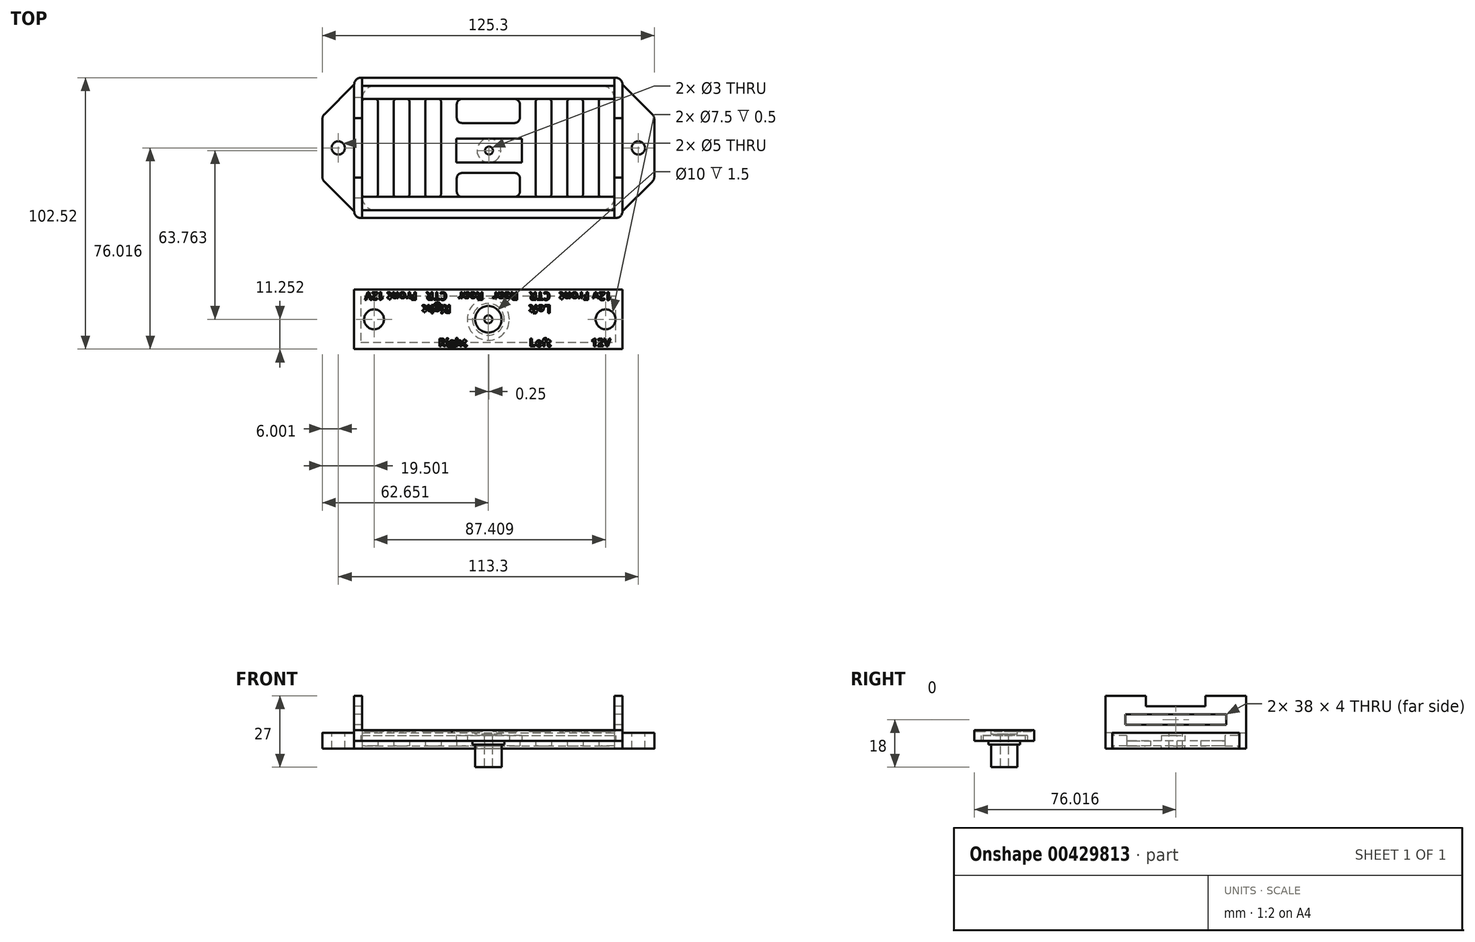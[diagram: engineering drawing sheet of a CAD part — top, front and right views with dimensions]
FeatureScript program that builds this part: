
annotation { "Feature Type Name" : "Feature", "Feature Type Description" : "" }
export const myFeature = defineFeature(function(context is Context, id is Id, definition is map)
    precondition{}
    {
        {
            var Q0;
            Q0=qCreatedBy(makeId("Top.planeOp"),FACE);
            var sketch = newSketch(context, id + "F0", { "sketchPlane" : qUnion([Q0])});
            skLineSegment(sketch, "E0.bottom", {"start": v(-46, 15.89) * mm, "end": v(49.3, 15.89) * mm});
            skLineSegment(sketch, "E0.top", {"start": v(-46, -31.11) * mm, "end": v(49.3, -31.11) * mm});
            skLineSegment(sketch, "E0.left", {"start": v(-46, 15.89) * mm, "end": v(-46, -31.11) * mm});
            skLineSegment(sketch, "E0.right", {"start": v(49.3, 15.89) * mm, "end": v(49.3, -31.11) * mm});
            skLineSegment(sketch, "E1.0", {"start": v(-46.46, -34.11) * mm, "end": v(49.76, -34.11) * mm});
            skLineSegment(sketch, "E1.1", {"start": v(-49, 16.35) * mm, "end": v(-49, -31.57) * mm});
            skLineSegment(sketch, "E1.2", {"start": v(-46.46, 18.89) * mm, "end": v(49.76, 18.89) * mm});
            skLineSegment(sketch, "E1.3", {"start": v(52.3, 16.35) * mm, "end": v(52.3, -31.57) * mm});
            skPoint(sketch, "E2.visualSharp", {"position": v(-49, 18.89) * mm});
            skArc(sketch, "E2.filletArc", {"start": v(-46.46, 18.89) * mm, "mid": v(-48.25, 18.14) * mm, "end": v(-49, 16.35) * mm});
            skPoint(sketch, "E3.visualSharp", {"position": v(-49, -34.11) * mm});
            skArc(sketch, "E3.filletArc", {"start": v(-49, -31.57) * mm, "mid": v(-48.25, -33.37) * mm, "end": v(-46.46, -34.11) * mm});
            skPoint(sketch, "E4.visualSharp", {"position": v(52.3, -34.11) * mm});
            skArc(sketch, "E4.filletArc", {"start": v(49.76, -34.11) * mm, "mid": v(51.56, -33.37) * mm, "end": v(52.3, -31.57) * mm});
            skPoint(sketch, "E5.visualSharp", {"position": v(52.3, 18.89) * mm});
            skArc(sketch, "E5.filletArc", {"start": v(52.3, 16.35) * mm, "mid": v(51.56, 18.14) * mm, "end": v(49.76, 18.89) * mm});
            skPoint(sketch, "E6.orphan", {"position": v(1.65, 15.89) * mm});
            skPoint(sketch, "E7.orphan", {"position": v(49.3, -7.61) * mm});
            skPoint(sketch, "E8.start.orphan", {"position": v(-46, -7.61) * mm});
            skLineSegment(sketch, "E9", {"start": v(14.3, -13.11) * mm, "end": v(14.3, -4.11) * mm});
            skLineSegment(sketch, "E10", {"start": v(-10.5, -4.11) * mm, "end": v(14.3, -4.11) * mm});
            skLineSegment(sketch, "E11", {"start": v(14.3, -13.11) * mm, "end": v(-10.5, -13.11) * mm});
            skLineSegment(sketch, "E12", {"start": v(-10.5, -4.11) * mm, "end": v(-10.5, -13.11) * mm});
            skLineSegment(sketch, "E13", {"start": v(-46, 10.89) * mm, "end": v(49.3, 10.89) * mm});
            skPoint(sketch, "E14.end.orphan", {"position": v(1.65, 10.89) * mm});
            skLineSegment(sketch, "E15", {"start": v(1.65, -31.11) * mm, "end": v(1.65, -26.11) * mm});
            skLineSegment(sketch, "E16", {"start": v(-46, -26.11) * mm, "end": v(49.3, -26.11) * mm});
            skLineSegment(sketch, "E17", {"start": v(49.3, 15.89) * mm, "end": v(49.3, 18.89) * mm});
            skLineSegment(sketch, "E18", {"start": v(-46, 15.89) * mm, "end": v(-46, 18.89) * mm});
            skLineSegment(sketch, "E19", {"start": v(49.3, -31.11) * mm, "end": v(49.3, -34.11) * mm});
            skLineSegment(sketch, "E20", {"start": v(-46, -31.11) * mm, "end": v(-46, -34.11) * mm});
            skCircle(sketch, "E21", {"center": v(1.9, -8.61) * mm, "radius": 1.5 * mm});
            skPoint(sketch, "E22.orphan", {"position": v(1.9, -13.11) * mm});
            skPoint(sketch, "E23.end.orphan", {"position": v(1.9, -4.11) * mm});
            skLineSegment(sketch, "E24.bottom", {"start": v(52.3, -61.13) * mm, "end": v(-49, -61.13) * mm});
            skLineSegment(sketch, "E24.top", {"start": v(52.3, -83.63) * mm, "end": v(-49, -83.63) * mm});
            skLineSegment(sketch, "E24.left", {"start": v(52.3, -61.13) * mm, "end": v(52.3, -83.63) * mm});
            skLineSegment(sketch, "E24.right", {"start": v(-49, -61.13) * mm, "end": v(-49, -83.63) * mm});
            skCircle(sketch, "E25", {"center": v(1.65, -72.38) * mm, "radius": 1.5 * mm});
            skPoint(sketch, "E26.orphan", {"position": v(1.65, -83.63) * mm});
            skPoint(sketch, "E27.orphan", {"position": v(1.65, -61.13) * mm});
            skCircle(sketch, "E28", {"center": v(1.65, -72.38) * mm, "radius": 5 * mm});
            skLineSegment(sketch, "E29.right", {"start": v(-61, 3.31) * mm, "end": v(-61, -18.54) * mm});
            skLineSegment(sketch, "E30.right", {"start": v(64.3, 3.31) * mm, "end": v(64.3, -7.61) * mm});
            skLineSegment(sketch, "E31", {"start": v(64.3, -7.61) * mm, "end": v(64.3, -18.54) * mm});
            skLineSegment(sketch, "E32", {"start": v(52.3, 16.35) * mm, "end": v(63.56, 5.1) * mm});
            skLineSegment(sketch, "E33", {"start": v(63.56, -20.34) * mm, "end": v(52.3, -31.57) * mm});
            skLineSegment(sketch, "E34", {"start": v(-49, 16.35) * mm, "end": v(-60.25, 5.1) * mm});
            skLineSegment(sketch, "E35", {"start": v(-60.25, -20.34) * mm, "end": v(-49, -31.57) * mm});
            skPoint(sketch, "E36.orphan", {"position": v(-61, 16.35) * mm});
            skPoint(sketch, "E29.top.end.orphan", {"position": v(-61, -31.57) * mm});
            skPoint(sketch, "E37.orphan", {"position": v(64.3, 16.35) * mm});
            skPoint(sketch, "E38.orphan", {"position": v(64.3, -31.57) * mm});
            skPoint(sketch, "E39.end.orphan", {"position": v(52.3, -7.61) * mm});
            skPoint(sketch, "E40.end.orphan", {"position": v(-49, -7.61) * mm});
            skPoint(sketch, "E41.visualSharp", {"position": v(64.3, 4.37) * mm});
            skArc(sketch, "E41.filletArc", {"start": v(64.3, 3.31) * mm, "mid": v(64.1, 4.29) * mm, "end": v(63.56, 5.1) * mm});
            skPoint(sketch, "E42.visualSharp", {"position": v(64.3, -19.6) * mm});
            skArc(sketch, "E42.filletArc", {"start": v(63.56, -20.34) * mm, "mid": v(64.1, -19.51) * mm, "end": v(64.3, -18.54) * mm});
            skPoint(sketch, "E43.start.orphan", {"position": v(-61, -7.61) * mm});
            skPoint(sketch, "E44.visualSharp", {"position": v(-61, 4.37) * mm});
            skArc(sketch, "E44.filletArc", {"start": v(-60.25, 5.1) * mm, "mid": v(-60.8, 4.29) * mm, "end": v(-61, 3.31) * mm});
            skPoint(sketch, "E45.visualSharp", {"position": v(-61, -19.6) * mm});
            skArc(sketch, "E45.filletArc", {"start": v(-61, -18.54) * mm, "mid": v(-60.8, -19.51) * mm, "end": v(-60.25, -20.34) * mm});
            skCircle(sketch, "E46", {"center": v(-55, -7.61) * mm, "radius": 2.5 * mm});
            skCircle(sketch, "E47", {"center": v(58.3, -7.61) * mm, "radius": 2.5 * mm});
            skSolve(sketch);
        }
        {
            var Q0;
            Q0=makeQuery(id+"F0.imprint","IMPRINT",FACE,{"disambiguationData":[TD([[makeQuery(id+"F0.imprint","IMPRINT",EDGE,{"derivedFrom":sQuery(id+"F0.wireOp",EDGE,"E0.bottom")}),-1.0]])]});
            var Q1;
            Q1=makeQuery(id+"F0.imprint","IMPRINT",FACE,{"disambiguationData":[TD([[makeQuery(id+"F0.imprint","IMPRINT",EDGE,{"derivedFrom":sQuery(id+"F0.wireOp",EDGE,"E0.bottom")}),1.0]])]});
            var Q2;
            Q2=makeQuery(id+"F0.imprint","IMPRINT",FACE,{"disambiguationData":[TD([[makeQuery(id+"F0.imprint","IMPRINT",EDGE,{"derivedFrom":sQuery(id+"F0.wireOp",EDGE,"269553c9-e765-4ec5-81e7-e4e1725ccf4f.0")}),-1.0]])]});
            var Q3;
            Q3=makeQuery(id+"F0.imprint","IMPRINT",FACE,{"disambiguationData":[TD([[makeQuery(id+"F0.imprint","IMPRINT",EDGE,{"derivedFrom":sQuery(id+"F0.wireOp",EDGE,"E9")}),1.0]])]});
            var Q4;
            Q4=makeQuery(id+"F0.imprint","IMPRINT",FACE,{"disambiguationData":[TD([[makeQuery(id+"F0.imprint","IMPRINT",EDGE,{"derivedFrom":sQuery(id+"F0.wireOp",EDGE,"E9")}),-1.0]])]});
            var Q5;
            {var subQ3=sQuery(id+"F0.wireOp",EDGE,"E15");Q5=makeQuery(id+"F0.imprint","IMPRINT",FACE,{"disambiguationData":[TD([[makeQuery(id+"F0.imprint","IMPRINT",EDGE,{"derivedFrom":subQ3}),1.0]])]});}
            var Q6;
            {var subQ3=sQuery(id+"F0.wireOp",EDGE,"E15");Q6=makeQuery(id+"F0.imprint","IMPRINT",FACE,{"disambiguationData":[TD([[makeQuery(id+"F0.imprint","IMPRINT",EDGE,{"derivedFrom":subQ3}),-1.0]])]});}
            var Q7;
            {var subQ0=sQuery(id+"F0.wireOp",EDGE,"E19");Q7=makeQuery(id+"F0.imprint","IMPRINT",FACE,{"disambiguationData":[TD([[makeQuery(id+"F0.imprint","IMPRINT",EDGE,{"derivedFrom":subQ0}),-1.0]])]});}
            var Q8;
            Q8=makeQuery(id+"F0.imprint","IMPRINT",FACE,{"disambiguationData":[TD([[makeQuery(id+"F0.imprint","IMPRINT",EDGE,{"derivedFrom":sQuery(id+"F0.wireOp",EDGE,"E1.3")}),-1.0]])]});
            var Q9;
            Q9=makeQuery(id+"F0.imprint","IMPRINT",FACE,{"disambiguationData":[TD([[makeQuery(id+"F0.imprint","IMPRINT",EDGE,{"derivedFrom":sQuery(id+"F0.wireOp",EDGE,"E1.1")}),1.0]])]});
            var Q10;
            {var subQ6=sQuery(id+"F0.wireOp",EDGE,"E2.filletArc");Q10=makeQuery(id+"F0.imprint","IMPRINT",FACE,{"disambiguationData":[TD([[makeQuery(id+"F0.imprint","IMPRINT",EDGE,{"derivedFrom":subQ6}),1.0]])]});}
            var Q11;
            {var subQ5=sQuery(id+"F0.wireOp",EDGE,"E4.filletArc");Q11=makeQuery(id+"F0.imprint","IMPRINT",FACE,{"disambiguationData":[TD([[makeQuery(id+"F0.imprint","IMPRINT",EDGE,{"derivedFrom":subQ5}),1.0]])]});}
            var Q12;
            Q12=makeQuery(id+"F0.imprint","IMPRINT",FACE,{"disambiguationData":[TD([[makeQuery(id+"F0.imprint","IMPRINT",EDGE,{"derivedFrom":sQuery(id+"F0.wireOp",EDGE,"E1.1")}),-1.0]])]});
            var Q13;
            Q13=makeQuery(id+"F0.imprint","IMPRINT",FACE,{"disambiguationData":[TD([[makeQuery(id+"F0.imprint","IMPRINT",EDGE,{"derivedFrom":sQuery(id+"F0.wireOp",EDGE,"E1.3")}),1.0]])]});
            extrude(context, id + "F1", {"entities" : qUnion([Q0, Q1, Q2, Q3, Q4, Q5, Q6, Q7, Q8, Q9, Q10, Q11, Q12, Q13]), "oppositeDirection" : true, "depth" : 3 * mm});
        }
        {
            var Q0;
            Q0=makeQuery(id+"F0.imprint","IMPRINT",FACE,{"disambiguationData":[TD([[makeQuery(id+"F0.imprint","IMPRINT",EDGE,{"derivedFrom":sQuery(id+"F0.wireOp",EDGE,"E1.3")}),-1.0]])]});
            var Q1;
            Q1=makeQuery(id+"F0.imprint","IMPRINT",FACE,{"disambiguationData":[TD([[makeQuery(id+"F0.imprint","IMPRINT",EDGE,{"derivedFrom":sQuery(id+"F0.wireOp",EDGE,"E1.1")}),1.0]])]});
            var Q2;
            {var subQ6=sQuery(id+"F0.wireOp",EDGE,"E2.filletArc");Q2=makeQuery(id+"F0.imprint","IMPRINT",FACE,{"disambiguationData":[TD([[makeQuery(id+"F0.imprint","IMPRINT",EDGE,{"derivedFrom":subQ6}),1.0]])]});}
            var Q3;
            {var subQ5=sQuery(id+"F0.wireOp",EDGE,"E4.filletArc");Q3=makeQuery(id+"F0.imprint","IMPRINT",FACE,{"disambiguationData":[TD([[makeQuery(id+"F0.imprint","IMPRINT",EDGE,{"derivedFrom":subQ5}),1.0]])]});}
            extrude(context, id + "F2", {"entities" : qUnion([Q0, Q1, Q2, Q3]), "operationType" : NewBodyOperationType.ADD, "depth" : 17 * mm});
        }
        {
            var Q0;
            Q0=makeQuery(id+"F0.imprint","IMPRINT",FACE,{"disambiguationData":[TD([[makeQuery(id+"F0.imprint","IMPRINT",EDGE,{"derivedFrom":sQuery(id+"F0.wireOp",EDGE,"E9")}),1.0]])]});
            var Q1;
            {var subQ0=sQuery(id+"F0.wireOp",EDGE,"E0.bottom");Q1=makeQuery(id+"F0.imprint","IMPRINT",FACE,{"disambiguationData":[TD([[makeQuery(id+"F0.imprint","IMPRINT",EDGE,{"derivedFrom":subQ0}),-1.0]])]});}
            var Q2;
            {var subQ3=sQuery(id+"F0.wireOp",EDGE,"E15");Q2=makeQuery(id+"F0.imprint","IMPRINT",FACE,{"disambiguationData":[TD([[makeQuery(id+"F0.imprint","IMPRINT",EDGE,{"derivedFrom":subQ3}),1.0]])]});}
            var Q3;
            {var subQ3=sQuery(id+"F0.wireOp",EDGE,"E15");Q3=makeQuery(id+"F0.imprint","IMPRINT",FACE,{"disambiguationData":[TD([[makeQuery(id+"F0.imprint","IMPRINT",EDGE,{"derivedFrom":subQ3}),-1.0]])]});}
            extrude(context, id + "F3", {"entities" : qUnion([Q0, Q1, Q2, Q3]), "operationType" : NewBodyOperationType.ADD, "depth" : 2 * mm});
        }
        {
            var Q0;
            Q0=makeQuery(id+"F0.imprint","IMPRINT",FACE,{"disambiguationData":[TD([[makeQuery(id+"F0.imprint","IMPRINT",EDGE,{"derivedFrom":sQuery(id+"F0.wireOp",EDGE,"E0.bottom")}),1.0]])]});
            var Q1;
            {var subQ0=sQuery(id+"F0.wireOp",EDGE,"E19");Q1=makeQuery(id+"F0.imprint","IMPRINT",FACE,{"disambiguationData":[TD([[makeQuery(id+"F0.imprint","IMPRINT",EDGE,{"derivedFrom":subQ0}),-1.0]])]});}
            extrude(context, id + "F4", {"entities" : qUnion([Q0, Q1]), "operationType" : NewBodyOperationType.ADD, "depth" : 3 * mm});
        }
        {
            var Q0;
            Q0=makeQuery(id+"F2.opExtrude","CAP_FACE",FACE,{"disambiguationData":[OSD([sQuery(id+"F0.wireOp",EDGE,"E0.right"),sQuery(id+"F0.wireOp",EDGE,"E1.0"),sQuery(id+"F0.wireOp",EDGE,"E1.2"),sQuery(id+"F0.wireOp",EDGE,"E1.3"),sQuery(id+"F0.wireOp",EDGE,"E4.filletArc"),sQuery(id+"F0.wireOp",EDGE,"E5.filletArc"),sQuery(id+"F0.wireOp",EDGE,"E17"),sQuery(id+"F0.wireOp",EDGE,"E19")])],"isStart":false});
            var sketch = newSketch(context, id + "F5", { "sketchPlane" : qUnion([Q0])});
            skPoint(sketch, "E48.orphan", {"position": v(49.3, -34.11) * mm});
            skPoint(sketch, "E49.orphan", {"position": v(52.3, -31.57) * mm});
            skPoint(sketch, "E50.1.start.orphan", {"position": v(52.3, 16.35) * mm});
            skPoint(sketch, "E50.0.end.orphan", {"position": v(49.3, 18.89) * mm});
            skLineSegment(sketch, "E51", {"start": v(52.3, -18.86) * mm, "end": v(52.3, 3.64) * mm});
            skLineSegment(sketch, "E52", {"start": v(52.3, 3.64) * mm, "end": v(49.3, 3.64) * mm});
            skLineSegment(sketch, "E53", {"start": v(49.3, -18.86) * mm, "end": v(52.3, -18.86) * mm});
            skPoint(sketch, "E54.end.orphan", {"position": v(52.3, -7.61) * mm});
            skPoint(sketch, "E55.start.orphan", {"position": v(49.3, -7.61) * mm});
            skLineSegment(sketch, "E56", {"start": v(49.3, -18.86) * mm, "end": v(49.3, 3.64) * mm});
            skSolve(sketch);
        }
        {
            var Q0;
            Q0=makeQuery(id+"F2.opExtrude","CAP_FACE",FACE,{"disambiguationData":[OSD([sQuery(id+"F0.wireOp",EDGE,"E0.left"),sQuery(id+"F0.wireOp",EDGE,"E1.0"),sQuery(id+"F0.wireOp",EDGE,"E1.1"),sQuery(id+"F0.wireOp",EDGE,"E1.2"),sQuery(id+"F0.wireOp",EDGE,"E2.filletArc"),sQuery(id+"F0.wireOp",EDGE,"E3.filletArc"),sQuery(id+"F0.wireOp",EDGE,"E18"),sQuery(id+"F0.wireOp",EDGE,"E20")])],"isStart":false});
            var sketch = newSketch(context, id + "F6", { "sketchPlane" : qUnion([Q0])});
            skLineSegment(sketch, "E57.0", {"start": v(-46, 18.89) * mm, "end": v(-46, -34.11) * mm});
            skLineSegment(sketch, "E58", {"start": v(-46, 3.64) * mm, "end": v(-49, 3.64) * mm});
            skLineSegment(sketch, "E59", {"start": v(-49, 3.64) * mm, "end": v(-49, -18.86) * mm});
            skLineSegment(sketch, "E60", {"start": v(-49, -18.86) * mm, "end": v(-46, -18.86) * mm});
            skPoint(sketch, "E61.end.orphan", {"position": v(-49, -7.61) * mm});
            skPoint(sketch, "E62.start.orphan", {"position": v(-46, -7.61) * mm});
            skLineSegment(sketch, "E63", {"start": v(-46, 3.64) * mm, "end": v(-46, -18.86) * mm});
            skSolve(sketch);
        }
        {
            var Q0;
            Q0=makeQuery(id+"F5.imprint","IMPRINT",FACE,{"disambiguationData":[TD([[makeQuery(id+"F5.imprint","IMPRINT",EDGE,{"derivedFrom":sQuery(id+"F5.wireOp",EDGE,"E51")}),-1.0]])]});
            var Q1;
            Q1=makeQuery(id+"F6.imprint","IMPRINT",FACE,{"disambiguationData":[TD([[makeQuery(id+"F6.imprint","IMPRINT",EDGE,{"derivedFrom":sQuery(id+"F6.wireOp",EDGE,"E58")}),1.0]])]});
            extrude(context, id + "F7", {"entities" : qUnion([Q0, Q1]), "operationType" : NewBodyOperationType.REMOVE, "oppositeDirection" : true, "depth" : 4 * mm});
        }
        {
            var Q0;
            Q0=makeQuery(id+"F0.imprint","IMPRINT",FACE,{"disambiguationData":[TD([[makeQuery(id+"F0.imprint","IMPRINT",EDGE,{"derivedFrom":sQuery(id+"F0.wireOp",EDGE,"E24.bottom")}),1.0]])]});
            var Q1;
            Q1=makeQuery(id+"F0.imprint","IMPRINT",FACE,{"disambiguationData":[TD([[makeQuery(id+"F0.imprint","IMPRINT",EDGE,{"derivedFrom":sQuery(id+"F0.wireOp",EDGE,"E25")}),-1.0]])]});
            extrude(context, id + "F8", {"entities" : qUnion([Q0, Q1]), "depth" : 4 * mm});
        }
        {
            var Q0;
            Q0=makeQuery(id+"F0.imprint","IMPRINT",FACE,{"disambiguationData":[TD([[makeQuery(id+"F0.imprint","IMPRINT",EDGE,{"derivedFrom":sQuery(id+"F0.wireOp",EDGE,"E25")}),-1.0]])]});
            extrude(context, id + "F9", {"entities" : qUnion([Q0]), "operationType" : NewBodyOperationType.ADD, "oppositeDirection" : true, "depth" : 10 * mm});
        }
        {
            var Q0;
            Q0=makeQuery(id+"F0.imprint","IMPRINT",FACE,{"disambiguationData":[TD([[makeQuery(id+"F0.imprint","IMPRINT",EDGE,{"derivedFrom":sQuery(id+"F0.wireOp",EDGE,"E1.1")}),-1.0]])]});
            var Q1;
            Q1=makeQuery(id+"F0.imprint","IMPRINT",FACE,{"disambiguationData":[TD([[makeQuery(id+"F0.imprint","IMPRINT",EDGE,{"derivedFrom":sQuery(id+"F0.wireOp",EDGE,"E1.3")}),1.0]])]});
            extrude(context, id + "F10", {"entities" : qUnion([Q0, Q1]), "operationType" : NewBodyOperationType.ADD, "depth" : 3 * mm});
        }
        {
            var Q0;
            Q0=makeQuery(id+"F8.opExtrude","CAP_FACE",FACE,{"disambiguationData":[OSD([sQuery(id+"F0.wireOp",EDGE,"E24.bottom"),sQuery(id+"F0.wireOp",EDGE,"E24.top"),sQuery(id+"F0.wireOp",EDGE,"E24.left"),sQuery(id+"F0.wireOp",EDGE,"E24.right"),sQuery(id+"F0.wireOp",EDGE,"E25")])],"isStart":false});
            var sketch = newSketch(context, id + "F11", { "sketchPlane" : qUnion([Q0])});
            skCircle(sketch, "E64.0", {"center": v(1.65, -72.38) * mm, "radius": 5 * mm});
            skSolve(sketch);
        }
        {
            var Q0;
            Q0=makeQuery(id+"F11.imprint","IMPRINT",FACE,{"disambiguationData":[TD([[makeQuery(id+"F11.imprint","IMPRINT",EDGE,{"derivedFrom":sQuery(id+"F11.wireOp",EDGE,"E64.0")}),1.0]])]});
            extrude(context, id + "F12", {"entities" : qUnion([Q0]), "operationType" : NewBodyOperationType.REMOVE, "oppositeDirection" : true, "depth" : 1.5 * mm});
        }
        {
            var Q0;
            Q0=makeQuery(id+"F0.imprint","IMPRINT",FACE,{"disambiguationData":[TD([[makeQuery(id+"F0.imprint","IMPRINT",EDGE,{"derivedFrom":sQuery(id+"F0.wireOp",EDGE,"E24.bottom")}),1.0]])]});
            var sketch = newSketch(context, id + "F13", { "sketchPlane" : qUnion([Q0])});
            skCircle(sketch, "E65.0", {"center": v(1.65, -72.38) * mm, "radius": 5 * mm});
            skCircle(sketch, "E66.0", {"center": v(1.65, -72.38) * mm, "radius": 6 * mm});
            skSolve(sketch);
        }
        {
            var Q0;
            Q0=makeQuery(id+"F13.imprint","IMPRINT",FACE,{"disambiguationData":[TD([[makeQuery(id+"F13.imprint","IMPRINT",EDGE,{"derivedFrom":sQuery(id+"F13.wireOp",EDGE,"E65.0")}),-1.0]])]});
            extrude(context, id + "F14", {"entities" : qUnion([Q0]), "operationType" : NewBodyOperationType.ADD, "oppositeDirection" : true, "depth" : 1.5 * mm});
        }
        {
            var Q0;
            Q0=makeQuery(id+"F8.opExtrude","CAP_FACE",FACE,{"disambiguationData":[OSD([sQuery(id+"F0.wireOp",EDGE,"E24.bottom"),sQuery(id+"F0.wireOp",EDGE,"E24.top"),sQuery(id+"F0.wireOp",EDGE,"E24.left"),sQuery(id+"F0.wireOp",EDGE,"E24.right"),sQuery(id+"F0.wireOp",EDGE,"E25")])],"isStart":false});
            var sketch = newSketch(context, id + "F15", { "sketchPlane" : qUnion([Q0])});
            skLineSegment(sketch, "E67", {"start": v(-49, -61.13) * mm, "end": v(-46, -61.13) * mm});
            skLineSegment(sketch, "E68", {"start": v(-46, -61.13) * mm, "end": v(-36, -61.13) * mm});
            skLineSegment(sketch, "E69", {"start": v(-36, -61.13) * mm, "end": v(-26, -61.13) * mm});
            skLineSegment(sketch, "E70", {"start": v(-26, -61.13) * mm, "end": v(-23, -61.13) * mm});
            skLineSegment(sketch, "E71", {"start": v(-23, -61.13) * mm, "end": v(-13, -61.13) * mm});
            skLineSegment(sketch, "E72", {"start": v(-13, -61.13) * mm, "end": v(-10, -61.13) * mm});
            skLineSegment(sketch, "E73", {"start": v(-10, -61.13) * mm, "end": v(0, -61.13) * mm});
            skLineSegment(sketch, "E74", {"start": v(0, -61.13) * mm, "end": v(3, -61.13) * mm});
            skLineSegment(sketch, "E75", {"start": v(3, -61.13) * mm, "end": v(13, -61.13) * mm});
            skLineSegment(sketch, "E76", {"start": v(13, -61.13) * mm, "end": v(16, -61.13) * mm});
            skLineSegment(sketch, "E77", {"start": v(16, -61.13) * mm, "end": v(26, -61.13) * mm});
            skLineSegment(sketch, "E78", {"start": v(26, -61.13) * mm, "end": v(29, -61.13) * mm});
            skLineSegment(sketch, "E79", {"start": v(29, -61.13) * mm, "end": v(39, -61.13) * mm});
            skLineSegment(sketch, "E80", {"start": v(39, -61.13) * mm, "end": v(49, -61.13) * mm});
            skLineSegment(sketch, "E81", {"start": v(52.3, -83.63) * mm, "end": v(49.3, -83.63) * mm});
            skLineSegment(sketch, "E82", {"start": v(49.3, -83.63) * mm, "end": v(39.3, -83.63) * mm});
            skLineSegment(sketch, "E83", {"start": v(39.3, -83.63) * mm, "end": v(26.3, -83.63) * mm});
            skLineSegment(sketch, "E84", {"start": v(26.3, -83.63) * mm, "end": v(16.3, -83.63) * mm});
            skLineSegment(sketch, "E85", {"start": v(16.3, -83.63) * mm, "end": v(-6.7, -83.63) * mm});
            skLineSegment(sketch, "E86", {"start": v(-6.7, -83.63) * mm, "end": v(-16.7, -83.63) * mm});
            skPoint(sketch, "E87.middle", {"position": v(44, -61.13) * mm});
            skText(sketch, "E88", { "text": "12v", "fontName": "OpenSans-Bold.ttf"});
            skPoint(sketch, "E89.start.orphan", {"position": v(34, -61.13) * mm});
            skPoint(sketch, "E90.start.orphan", {"position": v(21, -61.13) * mm});
            skLineSegment(sketch, "E91", {"start": v(44, -61.13) * mm, "end": v(44, -62.13) * mm});
            skLineSegment(sketch, "E92", {"start": v(34, -61.13) * mm, "end": v(34, -62.13) * mm});
            skLineSegment(sketch, "E93", {"start": v(21, -61.13) * mm, "end": v(21, -62.13) * mm});
            skPoint(sketch, "E94.start.orphan", {"position": v(-5, -61.13) * mm});
            skPoint(sketch, "E95.start.orphan", {"position": v(-41, -61.13) * mm});
            skPoint(sketch, "E96.start.orphan", {"position": v(-31, -61.13) * mm});
            skPoint(sketch, "E97.start.orphan", {"position": v(-18, -61.13) * mm});
            skPoint(sketch, "E98.start.orphan", {"position": v(8, -61.13) * mm});
            skLineSegment(sketch, "E99", {"start": v(8, -61.13) * mm, "end": v(8, -62.13) * mm});
            skLineSegment(sketch, "E100", {"start": v(-5, -61.13) * mm, "end": v(-5, -62.13) * mm});
            skLineSegment(sketch, "E101", {"start": v(-18, -61.13) * mm, "end": v(-18, -62.13) * mm});
            skLineSegment(sketch, "E102", {"start": v(-31, -61.13) * mm, "end": v(-31, -62.13) * mm});
            skLineSegment(sketch, "E103", {"start": v(-41, -61.13) * mm, "end": v(-41, -62.13) * mm});
            skLineSegment(sketch, "E104", {"start": v(34.62, -51.7) * mm, "end": v(26.62, -51.7) * mm});
            skLineSegment(sketch, "E105", {"start": v(26.62, -51.7) * mm, "end": v(26.62, -48.7) * mm});
            skText(sketch, "E106", { "text": "Front\n", "fontName": "OpenSans-Bold.ttf"});
            skText(sketch, "E107", { "text": "Rear", "fontName": "OpenSans-Bold.ttf"});
            skText(sketch, "E108", { "text": "CTR", "fontName": "OpenSans-Bold.ttf"});
            skLineSegment(sketch, "E109", {"start": v(21, -65.13) * mm, "end": v(21, -67) * mm});
            skText(sketch, "E110", { "text": "Left", "fontName": "OpenSans-Bold.ttf"});
            skText(sketch, "E111", { "text": "Rear", "fontName": "OpenSans-Bold.ttf"});
            skText(sketch, "E112", { "text": "CTR", "fontName": "OpenSans-Bold.ttf"});
            skText(sketch, "E113", { "text": "Front", "fontName": "OpenSans-Bold.ttf"});
            skText(sketch, "E114", { "text": "12V", "fontName": "OpenSans-Bold.ttf"});
            skLineSegment(sketch, "E115", {"start": v(-18, -65.13) * mm, "end": v(-18, -67) * mm});
            skText(sketch, "E116", { "text": "Right", "fontName": "OpenSans-Bold.ttf"});
            skText(sketch, "E117", { "text": "12V", "fontName": "OpenSans-Bold.ttf"});
            skLineSegment(sketch, "E118", {"start": v(44.3, -83.63) * mm, "end": v(44.3, -82.63) * mm});
            skLineSegment(sketch, "E119", {"start": v(21.3, -83.63) * mm, "end": v(21.3, -82.63) * mm});
            skLineSegment(sketch, "E120", {"start": v(-11.7, -83.63) * mm, "end": v(-11.7, -82.63) * mm});
            skText(sketch, "E121", { "text": "Left", "fontName": "OpenSans-Bold.ttf"});
            skText(sketch, "E122", { "text": "Right", "fontName": "OpenSans-Bold.ttf"});
            skLineSegment(sketch, "E123", {"start": v(26.3, -83.63) * mm, "end": v(39.3, -83.63) * mm});
            skLineSegment(sketch, "E124", {"start": v(32.8, -83.63) * mm, "end": v(32.8, -81.9) * mm});
            skLineSegment(sketch, "E125", {"start": v(32.8, -83.63) * mm, "end": v(27.8, -83.63) * mm});
            skLineSegment(sketch, "E126", {"start": v(32.8, -83.63) * mm, "end": v(37.8, -83.63) * mm});
            skLineSegment(sketch, "E127", {"start": v(27.8, -83.63) * mm, "end": v(27.8, -90.63) * mm});
            skLineSegment(sketch, "E128", {"start": v(37.8, -83.63) * mm, "end": v(37.8, -90.63) * mm});
            skLineSegment(sketch, "E129", {"start": v(37.8, -90.63) * mm, "end": v(27.8, -90.63) * mm});
            skLineSegment(sketch, "E130", {"start": v(4.8, -83.63) * mm, "end": v(4.8, -81.9) * mm});
            skLineSegment(sketch, "E131", {"start": v(4.8, -83.63) * mm, "end": v(-5.2, -83.63) * mm});
            skLineSegment(sketch, "E132", {"start": v(4.8, -83.63) * mm, "end": v(14.8, -83.63) * mm});
            skLineSegment(sketch, "E133", {"start": v(-49, -83.63) * mm, "end": v(-46, -83.63) * mm});
            skLineSegment(sketch, "E134", {"start": v(-46, -83.63) * mm, "end": v(-16.7, -83.63) * mm});
            skLineSegment(sketch, "E135", {"start": v(-31.35, -83.63) * mm, "end": v(-43.35, -83.63) * mm});
            skLineSegment(sketch, "E136", {"start": v(-31.35, -83.63) * mm, "end": v(-19.35, -83.63) * mm});
            skLineSegment(sketch, "E137", {"start": v(-43.35, -83.63) * mm, "end": v(-43.35, -90.63) * mm});
            skLineSegment(sketch, "E138", {"start": v(-19.35, -83.63) * mm, "end": v(-19.35, -90.63) * mm});
            skLineSegment(sketch, "E139", {"start": v(-19.35, -90.63) * mm, "end": v(-43.35, -90.63) * mm});
            skLineSegment(sketch, "E140", {"start": v(-5.2, -83.63) * mm, "end": v(-5.2, -90.63) * mm});
            skLineSegment(sketch, "E141", {"start": v(14.8, -83.63) * mm, "end": v(14.8, -90.63) * mm});
            skLineSegment(sketch, "E142", {"start": v(14.8, -90.63) * mm, "end": v(-5.2, -90.63) * mm});
            skLineSegment(sketch, "E143", {"start": v(-49, -72.38) * mm, "end": v(-41.5, -72.38) * mm});
            skPoint(sketch, "E143.endSnap0", {"position": v(-41.5, -63.61) * mm});
            skCircle(sketch, "E144", {"center": v(-41.5, -72.38) * mm, "radius": 3.75 * mm});
            skLineSegment(sketch, "E145", {"start": v(52.3, -72.38) * mm, "end": v(45.9, -72.38) * mm});
            skCircle(sketch, "E146", {"center": v(45.9, -72.38) * mm, "radius": 3.75 * mm});
            const initialGuessF15  = {"E88": [0.04828, -0.06213, -1, 0, 0.00306], "E106": [0.03972, -0.06213, -1, 0, 0.003], "E107": [0.0129, -0.06213, -1, 0, 0.003], "E108": [0.02505, -0.06213, -1, 0, 0.003], "E110": [0.02519, -0.067, -1, 0, 0.003], "E111": [-0.0001, -0.06213, -1, 0, 0.003], "E112": [-0.01395, -0.06213, -1, 0, 0.003], "E113": [-0.02528, -0.06213, -1, 0, 0.003], "E114": [-0.03775, -0.06216, -1, 0, 0.0029], "E116": [-0.01247, -0.067, -1, 0, 0.003], "E117": [0.04043, -0.08263, 1, 0, 0.003], "E121": [0.01711, -0.08263, 1, 0, 0.003], "E122": [-0.01723, -0.08263, 1, 0, 0.003]};
            skSetInitialGuess(sketch, initialGuessF15);
            skSolve(sketch);
        }
        {
            var Q0;
            Q0=makeQuery(id+"F15.imprint","IMPRINT",FACE,{"disambiguationData":[TD([[makeQuery(id+"F15.imprint","IMPRINT",EDGE,{"derivedFrom":sQuery(id+"F15.wireOp",EDGE,"E88.sketch_text.stroke-0")}),-1.0]])]});
            var Q1;
            {var subQ0=sQuery(id+"F15.wireOp",EDGE,"E88.sketch_text.stroke-11");Q1=makeQuery(id+"F15.imprint","IMPRINT",FACE,{"disambiguationData":[TD([[makeQuery(id+"F15.imprint","IMPRINT",EDGE,{"derivedFrom":subQ0}),-1.0]])]});}
            var Q2;
            Q2=makeQuery(id+"F15.imprint","IMPRINT",FACE,{"disambiguationData":[TD([[makeQuery(id+"F15.imprint","IMPRINT",EDGE,{"derivedFrom":sQuery(id+"F15.wireOp",EDGE,"E88.sketch_text.stroke-34")}),-1.0]])]});
            var Q3;
            Q3=makeQuery(id+"F15.imprint","IMPRINT",FACE,{"disambiguationData":[TD([[makeQuery(id+"F15.imprint","IMPRINT",EDGE,{"derivedFrom":sQuery(id+"F15.wireOp",EDGE,"E106.sketch_text.stroke-0")}),-1.0]])]});
            var Q4;
            Q4=makeQuery(id+"F15.imprint","IMPRINT",FACE,{"disambiguationData":[TD([[makeQuery(id+"F15.imprint","IMPRINT",EDGE,{"derivedFrom":sQuery(id+"F15.wireOp",EDGE,"E106.sketch_text.stroke-10")}),-1.0]])]});
            var Q5;
            Q5=makeQuery(id+"F15.imprint","IMPRINT",FACE,{"disambiguationData":[TD([[makeQuery(id+"F15.imprint","IMPRINT",EDGE,{"derivedFrom":sQuery(id+"F15.wireOp",EDGE,"E106.sketch_text.stroke-23")}),-1.0]])]});
            var Q6;
            Q6=makeQuery(id+"F15.imprint","IMPRINT",FACE,{"disambiguationData":[TD([[makeQuery(id+"F15.imprint","IMPRINT",EDGE,{"derivedFrom":sQuery(id+"F15.wireOp",EDGE,"E106.sketch_text.stroke-58")}),-1.0]])]});
            var Q7;
            Q7=makeQuery(id+"F15.imprint","IMPRINT",FACE,{"disambiguationData":[TD([[makeQuery(id+"F15.imprint","IMPRINT",EDGE,{"derivedFrom":sQuery(id+"F15.wireOp",EDGE,"E106.sketch_text.stroke-41")}),-1.0]])]});
            var Q8;
            Q8=makeQuery(id+"F15.imprint","IMPRINT",FACE,{"disambiguationData":[TD([[makeQuery(id+"F15.imprint","IMPRINT",EDGE,{"derivedFrom":sQuery(id+"F15.wireOp",EDGE,"E108.sketch_text.stroke-0")}),-1.0]])]});
            var Q9;
            Q9=makeQuery(id+"F15.imprint","IMPRINT",FACE,{"disambiguationData":[TD([[makeQuery(id+"F15.imprint","IMPRINT",EDGE,{"derivedFrom":sQuery(id+"F15.wireOp",EDGE,"E110.sketch_text.stroke-0")}),-1.0]])]});
            var Q10;
            Q10=makeQuery(id+"F15.imprint","IMPRINT",FACE,{"disambiguationData":[TD([[makeQuery(id+"F15.imprint","IMPRINT",EDGE,{"derivedFrom":sQuery(id+"F15.wireOp",EDGE,"E110.sketch_text.stroke-6")}),-1.0]])]});
            var Q11;
            {var subQ0=sQuery(id+"F15.wireOp",EDGE,"E108.sketch_text.stroke-16");Q11=makeQuery(id+"F15.imprint","IMPRINT",FACE,{"disambiguationData":[TD([[makeQuery(id+"F15.imprint","IMPRINT",EDGE,{"derivedFrom":subQ0}),-1.0]])]});}
            var Q12;
            Q12=makeQuery(id+"F15.imprint","IMPRINT",FACE,{"disambiguationData":[TD([[makeQuery(id+"F15.imprint","IMPRINT",EDGE,{"derivedFrom":sQuery(id+"F15.wireOp",EDGE,"E108.sketch_text.stroke-23")}),-1.0]])]});
            var Q13;
            Q13=makeQuery(id+"F15.imprint","IMPRINT",FACE,{"disambiguationData":[TD([[makeQuery(id+"F15.imprint","IMPRINT",EDGE,{"derivedFrom":sQuery(id+"F15.wireOp",EDGE,"E110.sketch_text.stroke-26")}),-1.0]])]});
            var Q14;
            Q14=makeQuery(id+"F15.imprint","IMPRINT",FACE,{"disambiguationData":[TD([[makeQuery(id+"F15.imprint","IMPRINT",EDGE,{"derivedFrom":sQuery(id+"F15.wireOp",EDGE,"E110.sketch_text.stroke-44")}),-1.0]])]});
            var Q15;
            Q15=makeQuery(id+"F15.imprint","IMPRINT",FACE,{"disambiguationData":[TD([[makeQuery(id+"F15.imprint","IMPRINT",EDGE,{"derivedFrom":sQuery(id+"F15.wireOp",EDGE,"E107.sketch_text.stroke-0")}),-1.0]])]});
            var Q16;
            Q16=makeQuery(id+"F15.imprint","IMPRINT",FACE,{"disambiguationData":[TD([[makeQuery(id+"F15.imprint","IMPRINT",EDGE,{"derivedFrom":sQuery(id+"F15.wireOp",EDGE,"E107.sketch_text.stroke-19")}),-1.0]])]});
            var Q17;
            Q17=makeQuery(id+"F15.imprint","IMPRINT",FACE,{"disambiguationData":[TD([[makeQuery(id+"F15.imprint","IMPRINT",EDGE,{"derivedFrom":sQuery(id+"F15.wireOp",EDGE,"E107.sketch_text.stroke-39")}),-1.0]])]});
            var Q18;
            Q18=makeQuery(id+"F15.imprint","IMPRINT",FACE,{"disambiguationData":[TD([[makeQuery(id+"F15.imprint","IMPRINT",EDGE,{"derivedFrom":sQuery(id+"F15.wireOp",EDGE,"E107.sketch_text.stroke-64")}),-1.0]])]});
            var Q19;
            Q19=makeQuery(id+"F15.imprint","IMPRINT",FACE,{"disambiguationData":[TD([[makeQuery(id+"F15.imprint","IMPRINT",EDGE,{"derivedFrom":sQuery(id+"F15.wireOp",EDGE,"E111.sketch_text.stroke-0")}),-1.0]])]});
            var Q20;
            Q20=makeQuery(id+"F15.imprint","IMPRINT",FACE,{"disambiguationData":[TD([[makeQuery(id+"F15.imprint","IMPRINT",EDGE,{"derivedFrom":sQuery(id+"F15.wireOp",EDGE,"E111.sketch_text.stroke-19")}),-1.0]])]});
            var Q21;
            Q21=makeQuery(id+"F15.imprint","IMPRINT",FACE,{"disambiguationData":[TD([[makeQuery(id+"F15.imprint","IMPRINT",EDGE,{"derivedFrom":sQuery(id+"F15.wireOp",EDGE,"E111.sketch_text.stroke-39")}),-1.0]])]});
            var Q22;
            Q22=makeQuery(id+"F15.imprint","IMPRINT",FACE,{"disambiguationData":[TD([[makeQuery(id+"F15.imprint","IMPRINT",EDGE,{"derivedFrom":sQuery(id+"F15.wireOp",EDGE,"E111.sketch_text.stroke-64")}),-1.0]])]});
            var Q23;
            Q23=makeQuery(id+"F15.imprint","IMPRINT",FACE,{"disambiguationData":[TD([[makeQuery(id+"F15.imprint","IMPRINT",EDGE,{"derivedFrom":sQuery(id+"F15.wireOp",EDGE,"E112.sketch_text.stroke-0")}),-1.0]])]});
            var Q24;
            {var subQ0=sQuery(id+"F15.wireOp",EDGE,"E112.sketch_text.stroke-16");Q24=makeQuery(id+"F15.imprint","IMPRINT",FACE,{"disambiguationData":[TD([[makeQuery(id+"F15.imprint","IMPRINT",EDGE,{"derivedFrom":subQ0}),-1.0]])]});}
            var Q25;
            Q25=makeQuery(id+"F15.imprint","IMPRINT",FACE,{"disambiguationData":[TD([[makeQuery(id+"F15.imprint","IMPRINT",EDGE,{"derivedFrom":sQuery(id+"F15.wireOp",EDGE,"E112.sketch_text.stroke-23")}),-1.0]])]});
            var Q26;
            Q26=makeQuery(id+"F15.imprint","IMPRINT",FACE,{"disambiguationData":[TD([[makeQuery(id+"F15.imprint","IMPRINT",EDGE,{"derivedFrom":sQuery(id+"F15.wireOp",EDGE,"E116.sketch_text.stroke-0")}),-1.0]])]});
            var Q27;
            Q27=makeQuery(id+"F15.imprint","IMPRINT",FACE,{"disambiguationData":[TD([[makeQuery(id+"F15.imprint","IMPRINT",EDGE,{"derivedFrom":sQuery(id+"F15.wireOp",EDGE,"E116.sketch_text.stroke-24")}),-1.0]])]});
            var Q28;
            Q28=makeQuery(id+"F15.imprint","IMPRINT",FACE,{"disambiguationData":[TD([[makeQuery(id+"F15.imprint","IMPRINT",EDGE,{"derivedFrom":sQuery(id+"F15.wireOp",EDGE,"E116.sketch_text.stroke-19")}),-1.0]])]});
            var Q29;
            Q29=makeQuery(id+"F15.imprint","IMPRINT",FACE,{"disambiguationData":[TD([[makeQuery(id+"F15.imprint","IMPRINT",EDGE,{"derivedFrom":sQuery(id+"F15.wireOp",EDGE,"E116.sketch_text.stroke-28")}),-1.0]])]});
            var Q30;
            Q30=makeQuery(id+"F15.imprint","IMPRINT",FACE,{"disambiguationData":[TD([[makeQuery(id+"F15.imprint","IMPRINT",EDGE,{"derivedFrom":sQuery(id+"F15.wireOp",EDGE,"E116.sketch_text.stroke-72")}),-1.0]])]});
            var Q31;
            Q31=makeQuery(id+"F15.imprint","IMPRINT",FACE,{"disambiguationData":[TD([[makeQuery(id+"F15.imprint","IMPRINT",EDGE,{"derivedFrom":sQuery(id+"F15.wireOp",EDGE,"E116.sketch_text.stroke-89")}),-1.0]])]});
            var Q32;
            Q32=makeQuery(id+"F15.imprint","IMPRINT",FACE,{"disambiguationData":[TD([[makeQuery(id+"F15.imprint","IMPRINT",EDGE,{"derivedFrom":sQuery(id+"F15.wireOp",EDGE,"E113.sketch_text.stroke-0")}),-1.0]])]});
            var Q33;
            Q33=makeQuery(id+"F15.imprint","IMPRINT",FACE,{"disambiguationData":[TD([[makeQuery(id+"F15.imprint","IMPRINT",EDGE,{"derivedFrom":sQuery(id+"F15.wireOp",EDGE,"E113.sketch_text.stroke-10")}),-1.0]])]});
            var Q34;
            Q34=makeQuery(id+"F15.imprint","IMPRINT",FACE,{"disambiguationData":[TD([[makeQuery(id+"F15.imprint","IMPRINT",EDGE,{"derivedFrom":sQuery(id+"F15.wireOp",EDGE,"E113.sketch_text.stroke-23")}),-1.0]])]});
            var Q35;
            Q35=makeQuery(id+"F15.imprint","IMPRINT",FACE,{"disambiguationData":[TD([[makeQuery(id+"F15.imprint","IMPRINT",EDGE,{"derivedFrom":sQuery(id+"F15.wireOp",EDGE,"E113.sketch_text.stroke-41")}),-1.0]])]});
            var Q36;
            Q36=makeQuery(id+"F15.imprint","IMPRINT",FACE,{"disambiguationData":[TD([[makeQuery(id+"F15.imprint","IMPRINT",EDGE,{"derivedFrom":sQuery(id+"F15.wireOp",EDGE,"E113.sketch_text.stroke-58")}),-1.0]])]});
            var Q37;
            Q37=makeQuery(id+"F15.imprint","IMPRINT",FACE,{"disambiguationData":[TD([[makeQuery(id+"F15.imprint","IMPRINT",EDGE,{"derivedFrom":sQuery(id+"F15.wireOp",EDGE,"E114.sketch_text.stroke-0")}),-1.0]])]});
            var Q38;
            {var subQ0=sQuery(id+"F15.wireOp",EDGE,"E114.sketch_text.stroke-11");Q38=makeQuery(id+"F15.imprint","IMPRINT",FACE,{"disambiguationData":[TD([[makeQuery(id+"F15.imprint","IMPRINT",EDGE,{"derivedFrom":subQ0}),-1.0]])]});}
            var Q39;
            Q39=makeQuery(id+"F15.imprint","IMPRINT",FACE,{"disambiguationData":[TD([[makeQuery(id+"F15.imprint","IMPRINT",EDGE,{"derivedFrom":sQuery(id+"F15.wireOp",EDGE,"E114.sketch_text.stroke-34")}),-1.0]])]});
            var Q40;
            Q40=makeQuery(id+"F15.imprint","IMPRINT",FACE,{"disambiguationData":[TD([[makeQuery(id+"F15.imprint","IMPRINT",EDGE,{"derivedFrom":sQuery(id+"F15.wireOp",EDGE,"E122.sketch_text.stroke-0")}),-1.0]])]});
            var Q41;
            Q41=makeQuery(id+"F15.imprint","IMPRINT",FACE,{"disambiguationData":[TD([[makeQuery(id+"F15.imprint","IMPRINT",EDGE,{"derivedFrom":sQuery(id+"F15.wireOp",EDGE,"E122.sketch_text.stroke-19")}),-1.0]])]});
            var Q42;
            Q42=makeQuery(id+"F15.imprint","IMPRINT",FACE,{"disambiguationData":[TD([[makeQuery(id+"F15.imprint","IMPRINT",EDGE,{"derivedFrom":sQuery(id+"F15.wireOp",EDGE,"E122.sketch_text.stroke-24")}),-1.0]])]});
            var Q43;
            Q43=makeQuery(id+"F15.imprint","IMPRINT",FACE,{"disambiguationData":[TD([[makeQuery(id+"F15.imprint","IMPRINT",EDGE,{"derivedFrom":sQuery(id+"F15.wireOp",EDGE,"E122.sketch_text.stroke-28")}),-1.0]])]});
            var Q44;
            Q44=makeQuery(id+"F15.imprint","IMPRINT",FACE,{"disambiguationData":[TD([[makeQuery(id+"F15.imprint","IMPRINT",EDGE,{"derivedFrom":sQuery(id+"F15.wireOp",EDGE,"E122.sketch_text.stroke-72")}),-1.0]])]});
            var Q45;
            Q45=makeQuery(id+"F15.imprint","IMPRINT",FACE,{"disambiguationData":[TD([[makeQuery(id+"F15.imprint","IMPRINT",EDGE,{"derivedFrom":sQuery(id+"F15.wireOp",EDGE,"E122.sketch_text.stroke-89")}),-1.0]])]});
            var Q46;
            Q46=makeQuery(id+"F15.imprint","IMPRINT",FACE,{"disambiguationData":[TD([[makeQuery(id+"F15.imprint","IMPRINT",EDGE,{"derivedFrom":sQuery(id+"F15.wireOp",EDGE,"E122.sketch_text.stroke-24")}),-1.0]])]});
            var Q47;
            Q47=makeQuery(id+"F15.imprint","IMPRINT",FACE,{"disambiguationData":[TD([[makeQuery(id+"F15.imprint","IMPRINT",EDGE,{"derivedFrom":sQuery(id+"F15.wireOp",EDGE,"E121.sketch_text.stroke-0")}),-1.0]])]});
            var Q48;
            Q48=makeQuery(id+"F15.imprint","IMPRINT",FACE,{"disambiguationData":[TD([[makeQuery(id+"F15.imprint","IMPRINT",EDGE,{"derivedFrom":sQuery(id+"F15.wireOp",EDGE,"E121.sketch_text.stroke-6")}),-1.0]])]});
            var Q49;
            Q49=makeQuery(id+"F15.imprint","IMPRINT",FACE,{"disambiguationData":[TD([[makeQuery(id+"F15.imprint","IMPRINT",EDGE,{"derivedFrom":sQuery(id+"F15.wireOp",EDGE,"E121.sketch_text.stroke-26")}),-1.0]])]});
            var Q50;
            Q50=makeQuery(id+"F15.imprint","IMPRINT",FACE,{"disambiguationData":[TD([[makeQuery(id+"F15.imprint","IMPRINT",EDGE,{"derivedFrom":sQuery(id+"F15.wireOp",EDGE,"E121.sketch_text.stroke-44")}),-1.0]])]});
            var Q51;
            Q51=makeQuery(id+"F15.imprint","IMPRINT",FACE,{"disambiguationData":[TD([[makeQuery(id+"F15.imprint","IMPRINT",EDGE,{"derivedFrom":sQuery(id+"F15.wireOp",EDGE,"E117.sketch_text.stroke-0")}),-1.0]])]});
            var Q52;
            {var subQ0=sQuery(id+"F15.wireOp",EDGE,"E117.sketch_text.stroke-11");Q52=makeQuery(id+"F15.imprint","IMPRINT",FACE,{"disambiguationData":[TD([[makeQuery(id+"F15.imprint","IMPRINT",EDGE,{"derivedFrom":subQ0}),-1.0]])]});}
            var Q53;
            Q53=makeQuery(id+"F15.imprint","IMPRINT",FACE,{"disambiguationData":[TD([[makeQuery(id+"F15.imprint","IMPRINT",EDGE,{"derivedFrom":sQuery(id+"F15.wireOp",EDGE,"E117.sketch_text.stroke-34")}),-1.0]])]});
            var Q54;
            Q54=makeQuery(id+"F15.imprint","IMPRINT",FACE,{"disambiguationData":[TD([[makeQuery(id+"F15.imprint","IMPRINT",EDGE,{"derivedFrom":sQuery(id+"F15.wireOp",EDGE,"E144")}),1.0]])]});
            var Q55;
            Q55=makeQuery(id+"F15.imprint","IMPRINT",FACE,{"disambiguationData":[TD([[makeQuery(id+"F15.imprint","IMPRINT",EDGE,{"derivedFrom":sQuery(id+"F15.wireOp",EDGE,"E146")}),1.0]])]});
            extrude(context, id + "F16", {"entities" : qUnion([Q0, Q1, Q2, Q3, Q4, Q5, Q6, Q7, Q8, Q9, Q10, Q11, Q12, Q13, Q14, Q15, Q16, Q17, Q18, Q19, Q20, Q21, Q22, Q23, Q24, Q25, Q26, Q27, Q28, Q29, Q30, Q31, Q32, Q33, Q34, Q35, Q36, Q37, Q38, Q39, Q40, Q41, Q42, Q43, Q44, Q45, Q46, Q47, Q48, Q49, Q50, Q51, Q52, Q53, Q54, Q55]), "operationType" : NewBodyOperationType.REMOVE, "oppositeDirection" : true, "depth" : .5 * mm});
        }
        {
            var Q0;
            Q0=makeQuery(id+"F1.opExtrude","CAP_FACE",FACE,{"disambiguationData":[OSD([sQuery(id+"F0.wireOp",EDGE,"E1.0"),sQuery(id+"F0.wireOp",EDGE,"E1.2"),sQuery(id+"F0.wireOp",EDGE,"E2.filletArc"),sQuery(id+"F0.wireOp",EDGE,"E3.filletArc"),sQuery(id+"F0.wireOp",EDGE,"E4.filletArc"),sQuery(id+"F0.wireOp",EDGE,"E5.filletArc"),sQuery(id+"F0.wireOp",EDGE,"E21"),sQuery(id+"F0.wireOp",EDGE,"E29.right"),sQuery(id+"F0.wireOp",EDGE,"E30.right"),sQuery(id+"F0.wireOp",EDGE,"E31"),sQuery(id+"F0.wireOp",EDGE,"E32"),sQuery(id+"F0.wireOp",EDGE,"E33"),sQuery(id+"F0.wireOp",EDGE,"E34"),sQuery(id+"F0.wireOp",EDGE,"E35"),sQuery(id+"F0.wireOp",EDGE,"E41.filletArc"),sQuery(id+"F0.wireOp",EDGE,"E42.filletArc"),sQuery(id+"F0.wireOp",EDGE,"E44.filletArc"),sQuery(id+"F0.wireOp",EDGE,"E45.filletArc"),sQuery(id+"F0.wireOp",EDGE,"E46"),sQuery(id+"F0.wireOp",EDGE,"E47")])],"isStart":false});
            var sketch = newSketch(context, id + "F17", { "sketchPlane" : qUnion([Q0])});
            skLineSegment(sketch, "E147.0", {"start": v(-41, -15.89) * mm, "end": v(44.3, -15.89) * mm});
            skLineSegment(sketch, "E147.1", {"start": v(49.3, -10.89) * mm, "end": v(49.3, 26.11) * mm});
            skLineSegment(sketch, "E147.2", {"start": v(-41, 31.11) * mm, "end": v(44.3, 31.11) * mm});
            skLineSegment(sketch, "E147.3", {"start": v(-46, -10.89) * mm, "end": v(-46, 26.11) * mm});
            skPoint(sketch, "E148.visualSharp", {"position": v(49.3, -15.89) * mm});
            skArc(sketch, "E148.filletArc", {"start": v(44.3, -15.89) * mm, "mid": v(47.84, -14.42) * mm, "end": v(49.3, -10.89) * mm});
            skPoint(sketch, "E149.visualSharp", {"position": v(49.3, 31.11) * mm});
            skArc(sketch, "E149.filletArc", {"start": v(49.3, 26.11) * mm, "mid": v(47.84, 29.65) * mm, "end": v(44.3, 31.11) * mm});
            skPoint(sketch, "E150.visualSharp", {"position": v(-46, 31.11) * mm});
            skArc(sketch, "E150.filletArc", {"start": v(-41, 31.11) * mm, "mid": v(-44.53, 29.65) * mm, "end": v(-46, 26.11) * mm});
            skPoint(sketch, "E151.visualSharp", {"position": v(-46, -15.89) * mm});
            skArc(sketch, "E151.filletArc", {"start": v(-46, -10.89) * mm, "mid": v(-44.53, -14.42) * mm, "end": v(-41, -15.89) * mm});
            skSolve(sketch);
        }
        {
            var Q0;
            Q0=makeQuery(id+"F17.imprint","IMPRINT",FACE,{"disambiguationData":[TD([[makeQuery(id+"F17.imprint","IMPRINT",EDGE,{"derivedFrom":sQuery(id+"F17.wireOp",EDGE,"E147.0")}),1.0]])]});
            extrude(context, id + "F18", {"entities" : qUnion([Q0]), "operationType" : NewBodyOperationType.REMOVE, "oppositeDirection" : true, "depth" : 1 * mm});
        }
        {
            var Q0;
            Q0=makeQuery(id+"F0.imprint","IMPRINT",FACE,{"disambiguationData":[TD([[makeQuery(id+"F0.imprint","IMPRINT",EDGE,{"derivedFrom":sQuery(id+"F0.wireOp",EDGE,"E24.bottom")}),1.0]])]});
            var sketch = newSketch(context, id + "F19", { "sketchPlane" : qUnion([Q0])});
            skLineSegment(sketch, "E152.0.0", {"start": v(-49, -83.63) * mm, "end": v(52.3, -83.63) * mm});
            skLineSegment(sketch, "E152.0.1", {"start": v(52.3, -83.63) * mm, "end": v(52.3, -61.13) * mm});
            skLineSegment(sketch, "E152.0.2", {"start": v(52.3, -61.13) * mm, "end": v(-49, -61.13) * mm});
            skLineSegment(sketch, "E152.0.3", {"start": v(-49, -61.13) * mm, "end": v(-49, -83.63) * mm});
            skCircle(sketch, "E153.0", {"center": v(1.65, -72.38) * mm, "radius": 6 * mm});
            skLineSegment(sketch, "E154.0", {"start": v(-46.46, -81.09) * mm, "end": v(49.76, -81.09) * mm});
            skLineSegment(sketch, "E154.1", {"start": v(-46.46, -63.67) * mm, "end": v(-46.46, -81.09) * mm});
            skLineSegment(sketch, "E154.2", {"start": v(49.76, -63.67) * mm, "end": v(-46.46, -63.67) * mm});
            skLineSegment(sketch, "E154.3", {"start": v(49.76, -81.09) * mm, "end": v(49.76, -63.67) * mm});
            skCircle(sketch, "E155.0", {"center": v(1.65, -72.38) * mm, "radius": 7.93 * mm});
            skSolve(sketch);
        }
        {
            var Q0;
            Q0=makeQuery(id+"F19.imprint","IMPRINT",FACE,{"disambiguationData":[TD([[makeQuery(id+"F19.imprint","IMPRINT",EDGE,{"derivedFrom":sQuery(id+"F19.wireOp",EDGE,"E154.0")}),1.0]])]});
            extrude(context, id + "F20", {"entities" : qUnion([Q0]), "operationType" : NewBodyOperationType.REMOVE, "depth" : 2 * mm});
        }
        {
            var Q0;
            Q0=makeQuery(id+"F18.boolean.opBoolean","COPY",FACE,{"derivedFrom":makeQuery(id+"F18.opExtrude","CAP_FACE",FACE,{"disambiguationData":[OSD([sQuery(id+"F0.wireOp",EDGE,"E21"),sQuery(id+"F17.wireOp",EDGE,"E147.0"),sQuery(id+"F17.wireOp",EDGE,"E147.1"),sQuery(id+"F17.wireOp",EDGE,"E147.2"),sQuery(id+"F17.wireOp",EDGE,"E147.3"),sQuery(id+"F17.wireOp",EDGE,"E148.filletArc"),sQuery(id+"F17.wireOp",EDGE,"E149.filletArc"),sQuery(id+"F17.wireOp",EDGE,"E150.filletArc"),sQuery(id+"F17.wireOp",EDGE,"E151.filletArc")])],"isStart":false})});
            var sketch = newSketch(context, id + "F21", { "sketchPlane" : qUnion([Q0])});
            skLineSegment(sketch, "E156.0", {"start": v(-45, -10.89) * mm, "end": v(-41.04, -10.89) * mm});
            skLineSegment(sketch, "E157.0", {"start": v(49.3, -9.89) * mm, "end": v(49.3, 25.11) * mm});
            skLineSegment(sketch, "E157.1", {"start": v(-46, -9.89) * mm, "end": v(-46, 25.11) * mm});
            skLineSegment(sketch, "E158", {"start": v(25.48, -9.89) * mm, "end": v(25.48, 25.11) * mm});
            skLineSegment(sketch, "E159", {"start": v(-22.17, -9.89) * mm, "end": v(-22.17, 25.11) * mm});
            skLineSegment(sketch, "E160", {"start": v(37.39, 25.11) * mm, "end": v(37.39, -9.89) * mm});
            skLineSegment(sketch, "E161", {"start": v(-34.09, 25.11) * mm, "end": v(-34.09, -9.89) * mm});
            skLineSegment(sketch, "E162", {"start": v(31.43, -9.89) * mm, "end": v(31.43, 25.11) * mm});
            skLineSegment(sketch, "E163", {"start": v(24.48, -10.89) * mm, "end": v(20.52, -10.89) * mm});
            skLineSegment(sketch, "E164", {"start": v(19.52, -9.89) * mm, "end": v(19.52, 25.11) * mm});
            skLineSegment(sketch, "E165", {"start": v(-16.22, -9.89) * mm, "end": v(-16.22, 25.11) * mm});
            skLineSegment(sketch, "E166", {"start": v(-29.13, -10.89) * mm, "end": v(-33.09, -10.89) * mm});
            skLineSegment(sketch, "E167", {"start": v(-28.13, -9.89) * mm, "end": v(-28.13, 25.11) * mm});
            skLineSegment(sketch, "E168", {"start": v(-40.04, -9.89) * mm, "end": v(-40.04, 25.11) * mm});
            skPoint(sketch, "E169.orphan", {"position": v(49.3, -10.89) * mm});
            skPoint(sketch, "E170.orphan", {"position": v(49.3, 26.11) * mm});
            skLineSegment(sketch, "E171", {"start": v(43.35, -9.89) * mm, "end": v(43.35, 25.11) * mm});
            skLineSegment(sketch, "E172.trimOffspring", {"start": v(-33.09, 26.11) * mm, "end": v(-29.13, 26.11) * mm});
            skPoint(sketch, "E156.1.start.orphan", {"position": v(-46, 26.11) * mm});
            skLineSegment(sketch, "E173", {"start": v(-45, 26.11) * mm, "end": v(-41.04, 26.11) * mm});
            skArc(sketch, "E174.filletArc", {"start": v(-45, 26.11) * mm, "mid": v(-45.7, 25.82) * mm, "end": v(-46, 25.11) * mm});
            skPoint(sketch, "E175.visualSharp", {"position": v(-40.04, 26.11) * mm});
            skArc(sketch, "E175.filletArc", {"start": v(-40.04, 25.11) * mm, "mid": v(-40.34, 25.82) * mm, "end": v(-41.04, 26.11) * mm});
            skLineSegment(sketch, "E176.trimOffspring", {"start": v(-21.17, -10.89) * mm, "end": v(-17.22, -10.89) * mm});
            skPoint(sketch, "E177.visualSharp", {"position": v(-46, -10.89) * mm});
            skArc(sketch, "E177.filletArc", {"start": v(-46, -9.89) * mm, "mid": v(-45.7, -10.6) * mm, "end": v(-45, -10.89) * mm});
            skPoint(sketch, "E178.visualSharp", {"position": v(-40.04, -10.89) * mm});
            skArc(sketch, "E178.filletArc", {"start": v(-41.04, -10.89) * mm, "mid": v(-40.34, -10.6) * mm, "end": v(-40.04, -9.89) * mm});
            skPoint(sketch, "E179.visualSharp", {"position": v(-34.09, -10.89) * mm});
            skArc(sketch, "E179.filletArc", {"start": v(-34.09, -9.89) * mm, "mid": v(-33.8, -10.6) * mm, "end": v(-33.09, -10.89) * mm});
            skPoint(sketch, "E180.visualSharp", {"position": v(-28.13, -10.89) * mm});
            skArc(sketch, "E180.filletArc", {"start": v(-29.13, -10.89) * mm, "mid": v(-28.42, -10.6) * mm, "end": v(-28.13, -9.89) * mm});
            skLineSegment(sketch, "E181.trimOffspring", {"start": v(-21.17, 26.11) * mm, "end": v(-17.22, 26.11) * mm});
            skPoint(sketch, "E182.visualSharp", {"position": v(-34.09, 26.11) * mm});
            skArc(sketch, "E182.filletArc", {"start": v(-33.09, 26.11) * mm, "mid": v(-33.8, 25.82) * mm, "end": v(-34.09, 25.11) * mm});
            skPoint(sketch, "E183.visualSharp", {"position": v(-28.13, 26.11) * mm});
            skArc(sketch, "E183.filletArc", {"start": v(-28.13, 25.11) * mm, "mid": v(-28.42, 25.82) * mm, "end": v(-29.13, 26.11) * mm});
            skPoint(sketch, "E184.visualSharp", {"position": v(-22.17, 26.11) * mm});
            skArc(sketch, "E184.filletArc", {"start": v(-21.17, 26.11) * mm, "mid": v(-21.88, 25.82) * mm, "end": v(-22.17, 25.11) * mm});
            skPoint(sketch, "E185.visualSharp", {"position": v(-16.22, 26.11) * mm});
            skArc(sketch, "E185.filletArc", {"start": v(-16.22, 25.11) * mm, "mid": v(-16.51, 25.82) * mm, "end": v(-17.22, 26.11) * mm});
            skPoint(sketch, "E186.visualSharp", {"position": v(-22.17, -10.89) * mm});
            skArc(sketch, "E186.filletArc", {"start": v(-22.17, -9.89) * mm, "mid": v(-21.88, -10.6) * mm, "end": v(-21.17, -10.89) * mm});
            skPoint(sketch, "E187.visualSharp", {"position": v(-16.22, -10.89) * mm});
            skArc(sketch, "E187.filletArc", {"start": v(-17.22, -10.89) * mm, "mid": v(-16.51, -10.6) * mm, "end": v(-16.22, -9.89) * mm});
            skLineSegment(sketch, "E188", {"start": v(20.52, 26.11) * mm, "end": v(24.48, 26.11) * mm});
            skLineSegment(sketch, "E189", {"start": v(32.43, 26.11) * mm, "end": v(36.39, 26.11) * mm});
            skLineSegment(sketch, "E190", {"start": v(44.35, 26.11) * mm, "end": v(48.3, 26.11) * mm});
            skLineSegment(sketch, "E191", {"start": v(44.35, -10.89) * mm, "end": v(48.3, -10.89) * mm});
            skLineSegment(sketch, "E192", {"start": v(36.39, -10.89) * mm, "end": v(32.43, -10.89) * mm});
            skPoint(sketch, "E193.visualSharp", {"position": v(19.52, 26.11) * mm});
            skArc(sketch, "E193.filletArc", {"start": v(20.52, 26.11) * mm, "mid": v(19.81, 25.82) * mm, "end": v(19.52, 25.11) * mm});
            skPoint(sketch, "E194.visualSharp", {"position": v(25.48, 26.11) * mm});
            skArc(sketch, "E194.filletArc", {"start": v(25.48, 25.11) * mm, "mid": v(25.18, 25.82) * mm, "end": v(24.48, 26.11) * mm});
            skPoint(sketch, "E195.visualSharp", {"position": v(19.52, -10.89) * mm});
            skArc(sketch, "E195.filletArc", {"start": v(19.52, -9.89) * mm, "mid": v(19.81, -10.6) * mm, "end": v(20.52, -10.89) * mm});
            skPoint(sketch, "E196.visualSharp", {"position": v(25.48, -10.89) * mm});
            skArc(sketch, "E196.filletArc", {"start": v(24.48, -10.89) * mm, "mid": v(25.18, -10.6) * mm, "end": v(25.48, -9.89) * mm});
            skPoint(sketch, "E197.visualSharp", {"position": v(31.43, -10.89) * mm});
            skArc(sketch, "E197.filletArc", {"start": v(31.43, -9.89) * mm, "mid": v(31.73, -10.6) * mm, "end": v(32.43, -10.89) * mm});
            skPoint(sketch, "E198.visualSharp", {"position": v(37.39, -10.89) * mm});
            skArc(sketch, "E198.filletArc", {"start": v(36.39, -10.89) * mm, "mid": v(37.1, -10.6) * mm, "end": v(37.39, -9.89) * mm});
            skPoint(sketch, "E199.visualSharp", {"position": v(31.43, 26.11) * mm});
            skArc(sketch, "E199.filletArc", {"start": v(32.43, 26.11) * mm, "mid": v(31.73, 25.82) * mm, "end": v(31.43, 25.11) * mm});
            skPoint(sketch, "E200.visualSharp", {"position": v(37.39, 26.11) * mm});
            skArc(sketch, "E200.filletArc", {"start": v(37.39, 25.11) * mm, "mid": v(37.1, 25.82) * mm, "end": v(36.39, 26.11) * mm});
            skPoint(sketch, "E201.visualSharp", {"position": v(43.35, 26.11) * mm});
            skArc(sketch, "E201.filletArc", {"start": v(44.35, 26.11) * mm, "mid": v(43.64, 25.82) * mm, "end": v(43.35, 25.11) * mm});
            skPoint(sketch, "E202.visualSharp", {"position": v(43.35, -10.89) * mm});
            skArc(sketch, "E202.filletArc", {"start": v(43.35, -9.89) * mm, "mid": v(43.64, -10.6) * mm, "end": v(44.35, -10.89) * mm});
            skArc(sketch, "E203.filletArc", {"start": v(48.3, -10.89) * mm, "mid": v(49, -10.6) * mm, "end": v(49.3, -9.89) * mm});
            skArc(sketch, "E204.filletArc", {"start": v(49.3, 25.11) * mm, "mid": v(49, 25.82) * mm, "end": v(48.3, 26.11) * mm});
            skPoint(sketch, "E205.start.orphan", {"position": v(-4.3, -10.89) * mm});
            skPoint(sketch, "E206.orphan", {"position": v(-10.26, 26.11) * mm});
            skPoint(sketch, "E207.orphan", {"position": v(1.65, 26.11) * mm});
            skPoint(sketch, "E208.start.orphan", {"position": v(7.6, -10.89) * mm});
            skPoint(sketch, "E209.start.orphan", {"position": v(13.56, 26.11) * mm});
            skPoint(sketch, "E210.orphan", {"position": v(1.65, -10.89) * mm});
            skPoint(sketch, "E211.end.orphan", {"position": v(-10.26, -10.89) * mm});
            skPoint(sketch, "E212.end.orphan", {"position": v(13.56, -10.89) * mm});
            skCircle(sketch, "E213.0", {"center": v(1.9, 8.61) * mm, "radius": 1.5 * mm});
            skCircle(sketch, "E214.0", {"center": v(1.9, 8.61) * mm, "radius": 4.5 * mm});
            skLineSegment(sketch, "E215.bottom", {"start": v(11.56, -10.89) * mm, "end": v(-8.26, -10.89) * mm});
            skLineSegment(sketch, "E215.top", {"start": v(11.56, -1.81) * mm, "end": v(-8.26, -1.81) * mm});
            skLineSegment(sketch, "E215.left", {"start": v(13.56, -8.89) * mm, "end": v(13.56, -3.81) * mm});
            skLineSegment(sketch, "E215.right", {"start": v(-10.26, -8.89) * mm, "end": v(-10.26, -3.81) * mm});
            skLineSegment(sketch, "E216.bottom", {"start": v(11.56, 26.11) * mm, "end": v(-8.26, 26.11) * mm});
            skLineSegment(sketch, "E216.top", {"start": v(11.56, 17.07) * mm, "end": v(-8.26, 17.07) * mm});
            skLineSegment(sketch, "E216.left", {"start": v(13.56, 24.11) * mm, "end": v(13.56, 19.07) * mm});
            skLineSegment(sketch, "E216.right", {"start": v(-10.26, 24.11) * mm, "end": v(-10.26, 19.07) * mm});
            skArc(sketch, "E217.filletArc", {"start": v(11.56, -10.89) * mm, "mid": v(12.98, -10.3) * mm, "end": v(13.56, -8.89) * mm});
            skPoint(sketch, "E218.visualSharp", {"position": v(13.56, -1.81) * mm});
            skArc(sketch, "E218.filletArc", {"start": v(13.56, -3.81) * mm, "mid": v(12.98, -2.4) * mm, "end": v(11.56, -1.81) * mm});
            skPoint(sketch, "E219.visualSharp", {"position": v(-10.26, -1.81) * mm});
            skArc(sketch, "E219.filletArc", {"start": v(-8.26, -1.81) * mm, "mid": v(-9.68, -2.4) * mm, "end": v(-10.26, -3.81) * mm});
            skArc(sketch, "E220.filletArc", {"start": v(-10.26, -8.89) * mm, "mid": v(-9.68, -10.3) * mm, "end": v(-8.26, -10.89) * mm});
            skPoint(sketch, "E221.visualSharp", {"position": v(13.56, 17.07) * mm});
            skArc(sketch, "E221.filletArc", {"start": v(11.56, 17.07) * mm, "mid": v(12.98, 17.66) * mm, "end": v(13.56, 19.07) * mm});
            skArc(sketch, "E222.filletArc", {"start": v(13.56, 24.11) * mm, "mid": v(12.98, 25.53) * mm, "end": v(11.56, 26.11) * mm});
            skPoint(sketch, "E223.visualSharp", {"position": v(-10.26, 17.07) * mm});
            skArc(sketch, "E223.filletArc", {"start": v(-10.26, 19.07) * mm, "mid": v(-9.68, 17.66) * mm, "end": v(-8.26, 17.07) * mm});
            skArc(sketch, "E224.filletArc", {"start": v(-8.26, 26.11) * mm, "mid": v(-9.68, 25.53) * mm, "end": v(-10.26, 24.11) * mm});
            skSolve(sketch);
        }
        {
            var Q0;
            {var subQ0=sQuery(id+"F21.wireOp",EDGE,"E157.0");Q0=makeQuery(id+"F21.imprint","IMPRINT",FACE,{"disambiguationData":[TD([[makeQuery(id+"F21.imprint","IMPRINT",EDGE,{"derivedFrom":subQ0}),1.0]])]});}
            var Q1;
            {var subQ0=sQuery(id+"F21.wireOp",EDGE,"E160");Q1=makeQuery(id+"F21.imprint","IMPRINT",FACE,{"disambiguationData":[TD([[makeQuery(id+"F21.imprint","IMPRINT",EDGE,{"derivedFrom":subQ0}),-1.0]])]});}
            var Q2;
            {var subQ0=sQuery(id+"F21.wireOp",EDGE,"E158");Q2=makeQuery(id+"F21.imprint","IMPRINT",FACE,{"disambiguationData":[TD([[makeQuery(id+"F21.imprint","IMPRINT",EDGE,{"derivedFrom":subQ0}),1.0]])]});}
            var Q3;
            {var subQ0=sQuery(id+"F21.wireOp",EDGE,"E159");Q3=makeQuery(id+"F21.imprint","IMPRINT",FACE,{"disambiguationData":[TD([[makeQuery(id+"F21.imprint","IMPRINT",EDGE,{"derivedFrom":subQ0}),-1.0]])]});}
            var Q4;
            {var subQ0=sQuery(id+"F21.wireOp",EDGE,"E161");Q4=makeQuery(id+"F21.imprint","IMPRINT",FACE,{"disambiguationData":[TD([[makeQuery(id+"F21.imprint","IMPRINT",EDGE,{"derivedFrom":subQ0}),1.0]])]});}
            var Q5;
            {var subQ0=sQuery(id+"F21.wireOp",EDGE,"E157.1");Q5=makeQuery(id+"F21.imprint","IMPRINT",FACE,{"disambiguationData":[TD([[makeQuery(id+"F21.imprint","IMPRINT",EDGE,{"derivedFrom":subQ0}),-1.0]])]});}
            var Q6;
            Q6=makeQuery(id+"F21.imprint","IMPRINT",FACE,{"disambiguationData":[TD([[makeQuery(id+"F21.imprint","IMPRINT",EDGE,{"derivedFrom":sQuery(id+"F21.wireOp",EDGE,"E216.bottom")}),1.0]])]});
            var Q7;
            Q7=makeQuery(id+"F21.imprint","IMPRINT",FACE,{"disambiguationData":[TD([[makeQuery(id+"F21.imprint","IMPRINT",EDGE,{"derivedFrom":sQuery(id+"F21.wireOp",EDGE,"E215.bottom")}),-1.0]])]});
            extrude(context, id + "F22", {"entities" : qUnion([Q0, Q1, Q2, Q3, Q4, Q5, Q6, Q7]), "operationType" : NewBodyOperationType.REMOVE, "oppositeDirection" : true, "depth" : 2 * mm});
        }
        {
            var Q0;
            Q0=makeQuery(id+"F2.opExtrude","SWEPT_FACE",FACE,{"disambiguationData":[OSD([sQuery(id+"F0.wireOp",EDGE,"E1.3")])]});
            var sketch = newSketch(context, id + "F23", { "sketchPlane" : qUnion([Q0])});
            skLineSegment(sketch, "E225.bottom", {"start": v(-26.61, 10) * mm, "end": v(11.39, 10) * mm});
            skLineSegment(sketch, "E225.top", {"start": v(-26.61, 6) * mm, "end": v(11.39, 6) * mm});
            skLineSegment(sketch, "E225.left", {"start": v(-26.61, 10) * mm, "end": v(-26.61, 6) * mm});
            skLineSegment(sketch, "E225.right", {"start": v(11.39, 10) * mm, "end": v(11.39, 6) * mm});
            skPoint(sketch, "E225.middle", {"position": v(-7.61, 8) * mm});
            skPoint(sketch, "E226.orphan", {"position": v(-7.61, 13) * mm});
            skPoint(sketch, "E227.end.orphan", {"position": v(-7.61, 3) * mm});
            skSolve(sketch);
        }
        {
            var Q0;
            Q0=makeQuery(id+"F2.opExtrude","SWEPT_FACE",FACE,{"disambiguationData":[OSD([sQuery(id+"F0.wireOp",EDGE,"E1.1")])]});
            var sketch = newSketch(context, id + "F24", { "sketchPlane" : qUnion([Q0])});
            skLineSegment(sketch, "E228.bottom", {"start": v(-11.39, 10) * mm, "end": v(26.61, 10) * mm});
            skLineSegment(sketch, "E228.top", {"start": v(-11.39, 6) * mm, "end": v(26.61, 6) * mm});
            skLineSegment(sketch, "E228.left", {"start": v(-11.39, 10) * mm, "end": v(-11.39, 6) * mm});
            skLineSegment(sketch, "E228.right", {"start": v(26.61, 10) * mm, "end": v(26.61, 6) * mm});
            skPoint(sketch, "E228.middle", {"position": v(7.61, 8) * mm});
            skPoint(sketch, "E229.orphan", {"position": v(7.61, 13) * mm});
            skPoint(sketch, "E230.end.orphan", {"position": v(7.61, 3) * mm});
            skSolve(sketch);
        }
        {
            var Q0;
            Q0=makeQuery(id+"F24.imprint","IMPRINT",FACE,{"disambiguationData":[TD([[makeQuery(id+"F24.imprint","IMPRINT",EDGE,{"derivedFrom":sQuery(id+"F24.wireOp",EDGE,"E228.bottom")}),-1.0]])]});
            var Q1;
            Q1=makeQuery(id+"F23.imprint","IMPRINT",FACE,{"disambiguationData":[TD([[makeQuery(id+"F23.imprint","IMPRINT",EDGE,{"derivedFrom":sQuery(id+"F23.wireOp",EDGE,"E225.bottom")}),-1.0]])]});
            extrude(context, id + "F25", {"entities" : qUnion([Q0, Q1]), "operationType" : NewBodyOperationType.REMOVE, "endBound" : BoundingType.SYMMETRIC, "oppositeDirection" : true, "depth" : 11 * mm});
        }
        {
            var Q0;
            Q0=makeQuery(id+"F21.imprint","IMPRINT",FACE,{"disambiguationData":[TD([[makeQuery(id+"F21.imprint","IMPRINT",EDGE,{"derivedFrom":sQuery(id+"F21.wireOp",EDGE,"E213.0")}),1.0]])]});
            var Q1;
            Q1=makeQuery(id+"F1.opExtrude","CAP_FACE",FACE,{"disambiguationData":[OSD([sQuery(id+"F0.wireOp",EDGE,"E1.0"),sQuery(id+"F0.wireOp",EDGE,"E1.2"),sQuery(id+"F0.wireOp",EDGE,"E2.filletArc"),sQuery(id+"F0.wireOp",EDGE,"E3.filletArc"),sQuery(id+"F0.wireOp",EDGE,"E4.filletArc"),sQuery(id+"F0.wireOp",EDGE,"E5.filletArc"),sQuery(id+"F0.wireOp",EDGE,"E21"),sQuery(id+"F0.wireOp",EDGE,"E29.right"),sQuery(id+"F0.wireOp",EDGE,"E30.right"),sQuery(id+"F0.wireOp",EDGE,"E31"),sQuery(id+"F0.wireOp",EDGE,"E32"),sQuery(id+"F0.wireOp",EDGE,"E33"),sQuery(id+"F0.wireOp",EDGE,"E34"),sQuery(id+"F0.wireOp",EDGE,"E35"),sQuery(id+"F0.wireOp",EDGE,"E41.filletArc"),sQuery(id+"F0.wireOp",EDGE,"E42.filletArc"),sQuery(id+"F0.wireOp",EDGE,"E44.filletArc"),sQuery(id+"F0.wireOp",EDGE,"E45.filletArc"),sQuery(id+"F0.wireOp",EDGE,"E46"),sQuery(id+"F0.wireOp",EDGE,"E47")])],"isStart":false});
            extrude(context, id + "F26", {"entities" : qUnion([Q0]), "operationType" : NewBodyOperationType.ADD, "endBound" : BoundingType.UP_TO_SURFACE, "endBoundEntityFace" : qUnion([Q1]), "depth" : 25 * mm});
        }
    });
